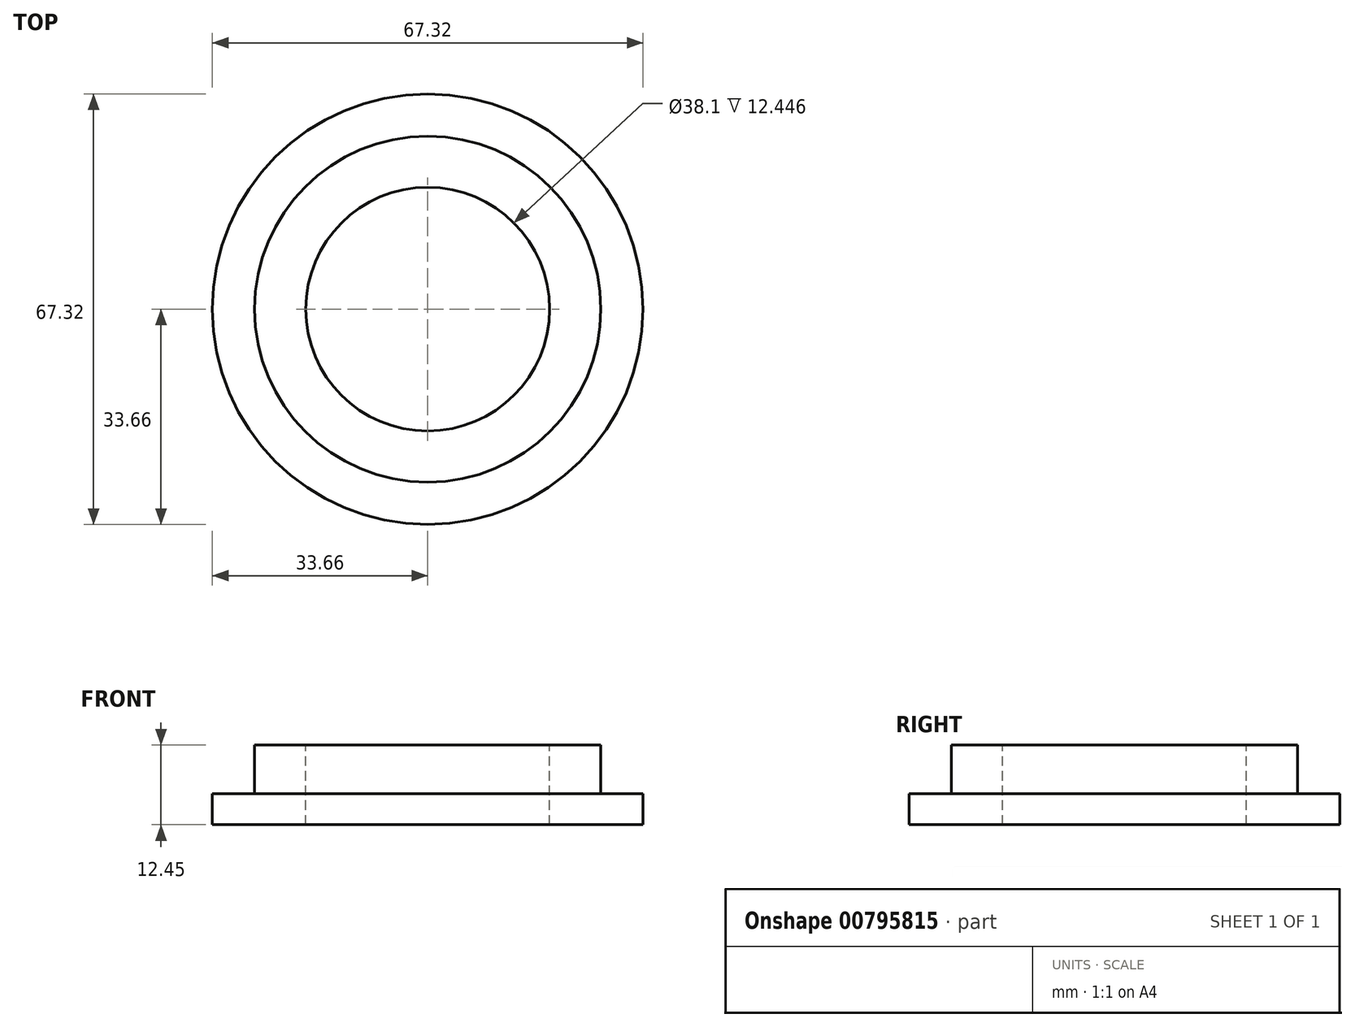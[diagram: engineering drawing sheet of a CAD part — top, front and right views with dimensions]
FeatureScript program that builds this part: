
annotation { "Feature Type Name" : "Feature", "Feature Type Description" : "" }
export const myFeature = defineFeature(function(context is Context, id is Id, definition is map)
    precondition{}
    {
        {
            var Q0;
            Q0=qCreatedBy(makeId("Top.planeOp"),FACE);
            var sketch = newSketch(context, id + "F0", { "sketchPlane" : qUnion([Q0])});
            skCircle(sketch, "E0", {"center": v(0, 0) * mm, "radius": 33.66 * mm});
            skSolve(sketch);
        }
        {
            var Q0;
            Q0 = qSketchRegion(id + "F0", true);
            extrude(context, id + "F1", {"entities" : qUnion([Q0]), "oppositeDirection" : true, "depth" : 4.83 * mm, "offsetDistance" : 25.4 * mm});
        }
        {
            var Q0;
            Q0=qCreatedBy(makeId("Top.planeOp"),FACE);
            var sketch = newSketch(context, id + "F2", { "sketchPlane" : qUnion([Q0])});
            skCircle(sketch, "E1", {"center": v(0, 0) * mm, "radius": 27.05 * mm});
            skSolve(sketch);
        }
        {
            var Q0;
            Q0 = qSketchRegion(id + "F2", true);
            extrude(context, id + "F3", {"entities" : qUnion([Q0]), "operationType" : NewBodyOperationType.ADD, "depth" : 7.62 * mm, "offsetDistance" : 25.4 * mm});
        }
        {
            var Q0;
            Q0=makeQuery(id+"F3.opExtrude","CAP_FACE",FACE,{"disambiguationData":[OSD([sQuery(id+"F2.wireOp",EDGE,"E1")])],"isStart":false});
            var sketch = newSketch(context, id + "F4", { "sketchPlane" : qUnion([Q0])});
            skCircle(sketch, "E2", {"center": v(0, 0) * mm, "radius": 19.05 * mm});
            skSolve(sketch);
        }
        {
            var Q0;
            Q0 = qSketchRegion(id + "F4", true);
            extrude(context, id + "F5", {"entities" : qUnion([Q0]), "operationType" : NewBodyOperationType.REMOVE, "endBound" : BoundingType.THROUGH_ALL, "oppositeDirection" : true, "depth" : 25.4 * mm, "offsetDistance" : 25.4 * mm});
        }
    });
